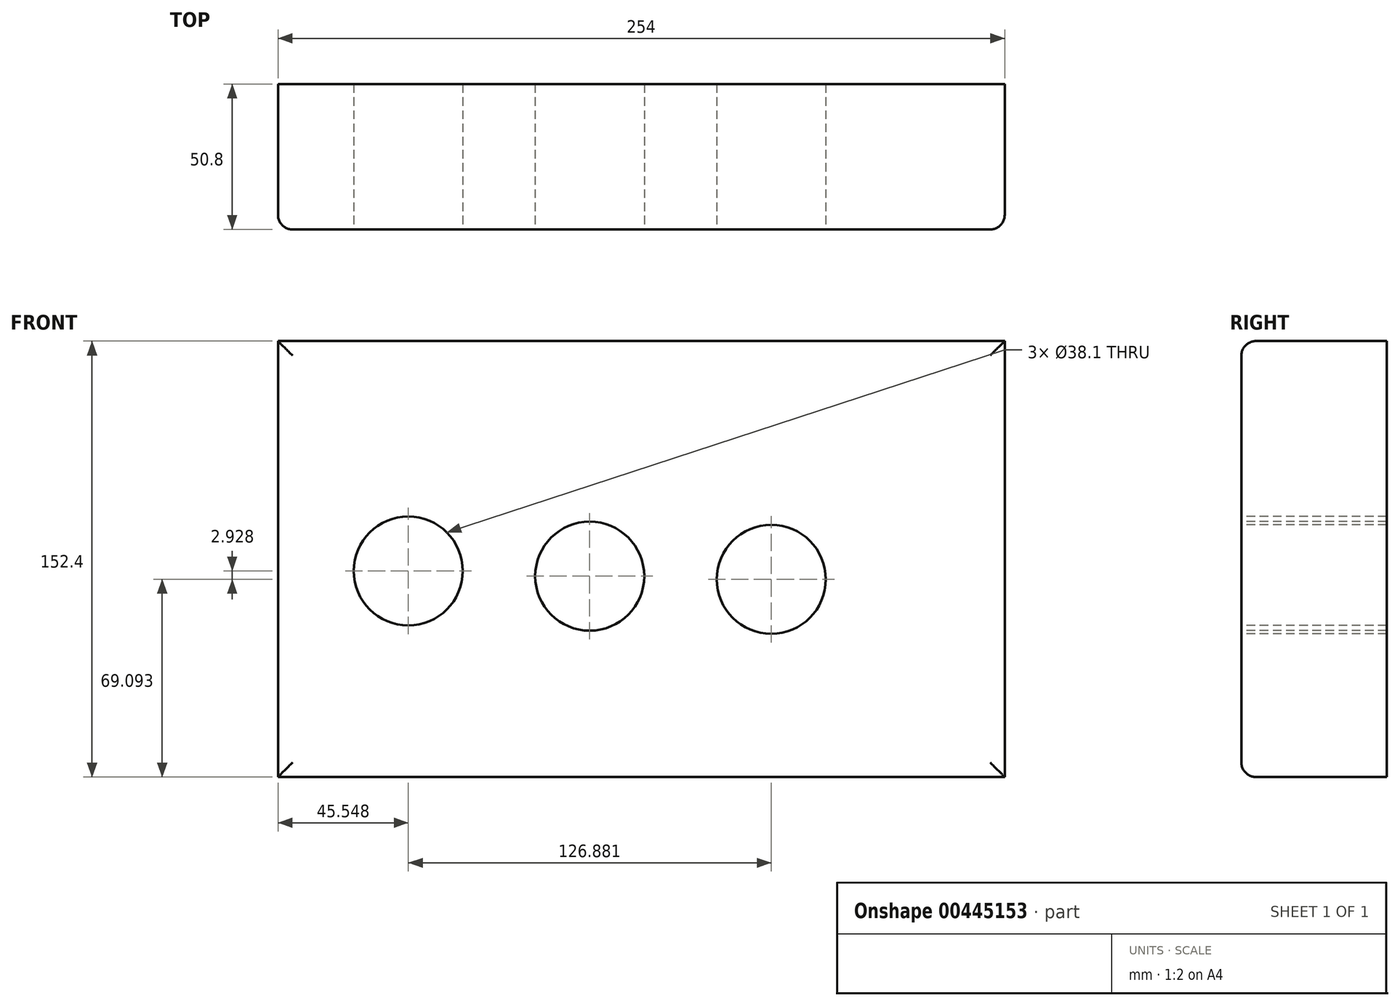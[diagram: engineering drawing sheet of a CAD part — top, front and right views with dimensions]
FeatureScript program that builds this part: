
annotation { "Feature Type Name" : "Feature", "Feature Type Description" : "" }
export const myFeature = defineFeature(function(context is Context, id is Id, definition is map)
    precondition{}
    {
        {
            var Q0;
            Q0=qCreatedBy(makeId("Front.planeOp"),FACE);
            var sketch = newSketch(context, id + "F0", { "sketchPlane" : qUnion([Q0])});
            skLineSegment(sketch, "E0.bottom", {"start": v(157.62, 82.2) * mm, "end": v(-96.38, 82.2) * mm});
            skLineSegment(sketch, "E0.top", {"start": v(157.62, -70.2) * mm, "end": v(-96.38, -70.2) * mm});
            skLineSegment(sketch, "E0.left", {"start": v(157.62, 82.2) * mm, "end": v(157.62, -70.2) * mm});
            skLineSegment(sketch, "E0.right", {"start": v(-96.38, 82.2) * mm, "end": v(-96.38, -70.2) * mm});
            skSolve(sketch);
        }
        {
            var Q0;
            Q0 = qSketchRegion(id + "F0", true);
            extrude(context, id + "F1", {"entities" : qUnion([Q0]), "depth" : 50.8 * mm});
        }
        {
            var Q0;
            Q0=makeQuery(id+"F1.opExtrude","CAP_FACE",FACE,{"disambiguationData":[OSD([sQuery(id+"F0.wireOp",EDGE,"E0.bottom"),sQuery(id+"F0.wireOp",EDGE,"E0.top"),sQuery(id+"F0.wireOp",EDGE,"E0.left"),sQuery(id+"F0.wireOp",EDGE,"E0.right")])],"isStart":false});
            var sketch = newSketch(context, id + "F2", { "sketchPlane" : qUnion([Q0])});
            skCircle(sketch, "E1", {"center": v(12.58, 0) * mm, "radius": 19.05 * mm});
            skLineSegment(sketch, "E2", {"start": v(-6.47, 0) * mm, "end": v(-31.87, 0) * mm});
            skCircle(sketch, "E3", {"center": v(-50.83, 1.81) * mm, "radius": 19.05 * mm});
            skPoint(sketch, "E3.second.point", {"position": v(-69.8, 0) * mm});
            skPoint(sketch, "E3.third.point", {"position": v(-52.7, -17.15) * mm});
            skLineSegment(sketch, "E4", {"start": v(31.63, 0) * mm, "end": v(57.03, 0) * mm});
            skCircle(sketch, "E5", {"center": v(76.05, -1.12) * mm, "radius": 19.05 * mm});
            skPoint(sketch, "E5.second.point", {"position": v(95.07, 0) * mm});
            skPoint(sketch, "E5.third.point", {"position": v(85.68, -17.55) * mm});
            skSolve(sketch);
        }
        {
            var Q0;
            Q0 = qSketchRegion(id + "F2", true);
            extrude(context, id + "F3", {"entities" : qUnion([Q0]), "operationType" : NewBodyOperationType.REMOVE, "oppositeDirection" : true, "depth" : 123.19 * mm});
        }
        {
            var Q0;
            Q0=makeQuery(id+"F1.opExtrude","CAP_EDGE",EDGE,{"disambiguationData":[OSD([sQuery(id+"F0.wireOp",EDGE,"E0.top")])],"isStart":false});
            var Q1;
            Q1=makeQuery(id+"F1.opExtrude","CAP_EDGE",EDGE,{"disambiguationData":[OSD([sQuery(id+"F0.wireOp",EDGE,"E0.left")])],"isStart":false});
            var Q2;
            Q2=makeQuery(id+"F1.opExtrude","CAP_EDGE",EDGE,{"disambiguationData":[OSD([sQuery(id+"F0.wireOp",EDGE,"E0.bottom")])],"isStart":false});
            var Q3;
            Q3=makeQuery(id+"F1.opExtrude","CAP_EDGE",EDGE,{"disambiguationData":[OSD([sQuery(id+"F0.wireOp",EDGE,"E0.right")])],"isStart":false});
            fillet(context, id + "F4", {"entities" : qUnion([Q0, Q1, Q2, Q3]), "radius" : 5.08 * mm, "tangentPropagation" : true, "allowEdgeOverflow" : false});
        }
    });
